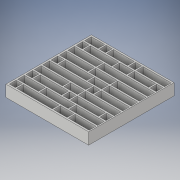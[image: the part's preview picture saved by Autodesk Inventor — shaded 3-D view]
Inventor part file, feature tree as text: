
AUTODESK INVENTOR PART (.ipt)
format: ipt  version: 2017 (Build 210142000, 142)  size: 391,680 bytes
history: native  units: mm
features: extrude x1, sketch x1
ambient origin geometry x8: Origin, YZ Plane, XZ Plane, XY Plane, X Axis, Y Axis, Z Axis, Center Point
bodies: Body1 (feature_tree)
feature tree (2):
  extrude  "Extrusion3"  Depth=12.8mm
  sketch  "Skizze1"  dims[d9=3.0mm d10=110.0mm d12=12.8mm d13=100.0mm d15=14.5mm d25=0.0mm]
